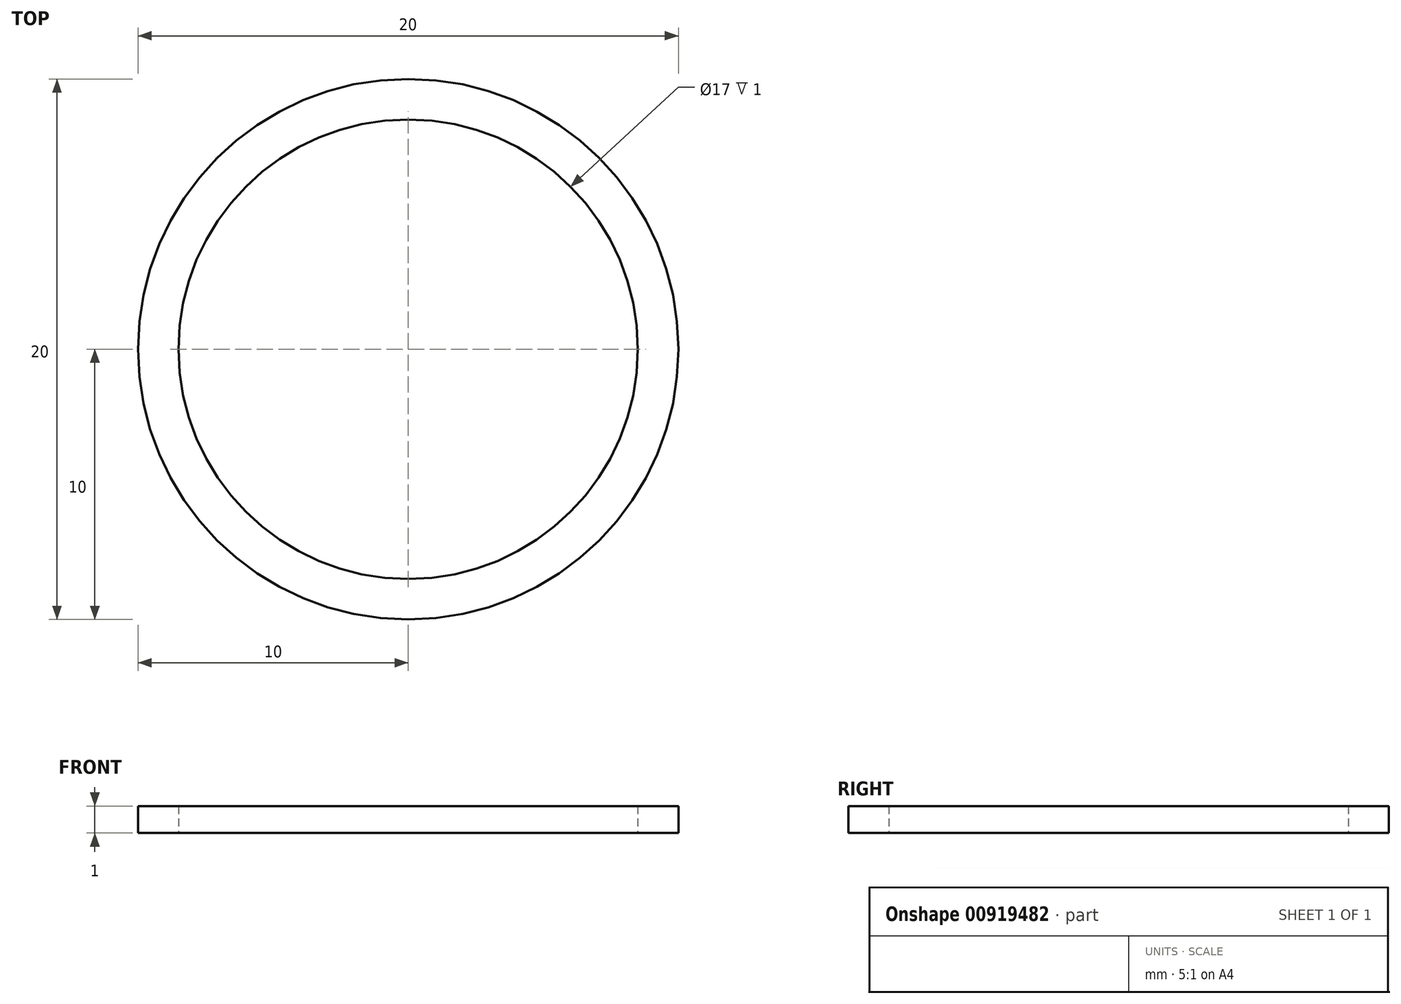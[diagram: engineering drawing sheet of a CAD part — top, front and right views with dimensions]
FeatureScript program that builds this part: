
annotation { "Feature Type Name" : "Feature", "Feature Type Description" : "" }
export const myFeature = defineFeature(function(context is Context, id is Id, definition is map)
    precondition{}
    {
        {
            var Q0;
            Q0=qCreatedBy(makeId("Top.planeOp"),FACE);
            var sketch = newSketch(context, id + "F0", { "sketchPlane" : qUnion([Q0])});
            skCircle(sketch, "E0", {"center": v(0, 0) * mm, "radius": 10 * mm});
            skCircle(sketch, "E1.0", {"center": v(0, 0) * mm, "radius": 8.5 * mm});
            skSolve(sketch);
        }
        {
            var Q0;
            Q0 = qSketchRegion(id + "F0", true);
            extrude(context, id + "F1", {"entities" : qUnion([Q0]), "depth" : 1 * mm, "offsetDistance" : 25 * mm});
        }
    });
